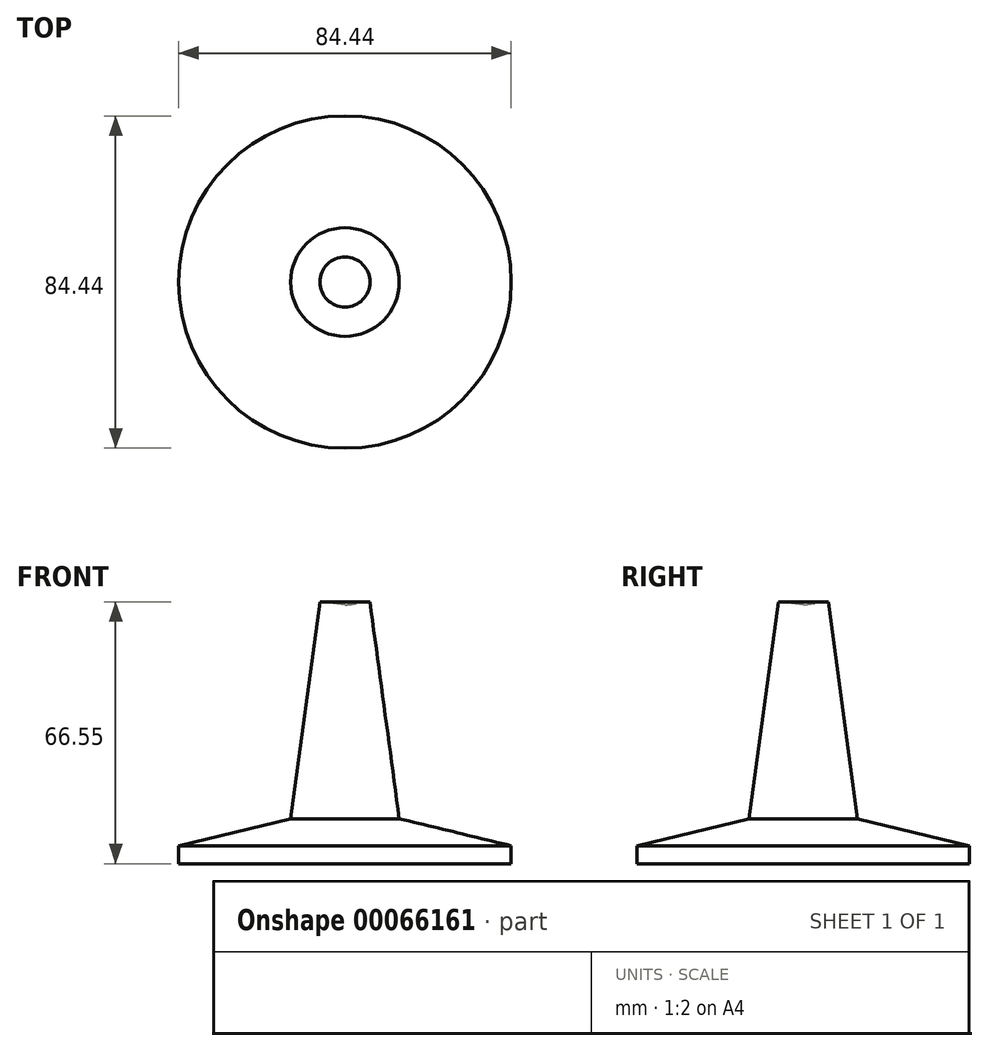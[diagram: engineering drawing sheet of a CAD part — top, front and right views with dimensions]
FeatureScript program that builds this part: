
annotation { "Feature Type Name" : "Feature", "Feature Type Description" : "" }
export const myFeature = defineFeature(function(context is Context, id is Id, definition is map)
    precondition{}
    {
        {
            var Q0;
            Q0=qCreatedBy(makeId("Front.planeOp"),FACE);
            var sketch = newSketch(context, id + "F0", { "sketchPlane" : qUnion([Q0])});
            skLineSegment(sketch, "E0", {"start": v(0, 0) * mm, "end": v(-42.22, 0) * mm});
            skLineSegment(sketch, "E1", {"start": v(-42.22, 0) * mm, "end": v(-42.22, 4.55) * mm});
            skLineSegment(sketch, "E2", {"start": v(-42.22, 4.55) * mm, "end": v(-13.8, 11.43) * mm});
            skLineSegment(sketch, "E3", {"start": v(-13.8, 11.43) * mm, "end": v(-6.35, 66.55) * mm});
            skLineSegment(sketch, "E4", {"start": v(-6.35, 66.55) * mm, "end": v(0, 65.7) * mm});
            skLineSegment(sketch, "E5", {"start": v(0, 65.7) * mm, "end": v(0, 0) * mm});
            skSolve(sketch);
        }
        {
            var Q0;
            Q0 = qSketchRegion(id + "F0", true);
            var Q1;
            Q1=sQuery(id+"F0.wireOp",EDGE,"E5");
            revolve(context, id + "F1", {"entities" : qUnion([Q0]), "axis" : qUnion([Q1]), "revolveType" : RevolveType.FULL});
        }
    });
